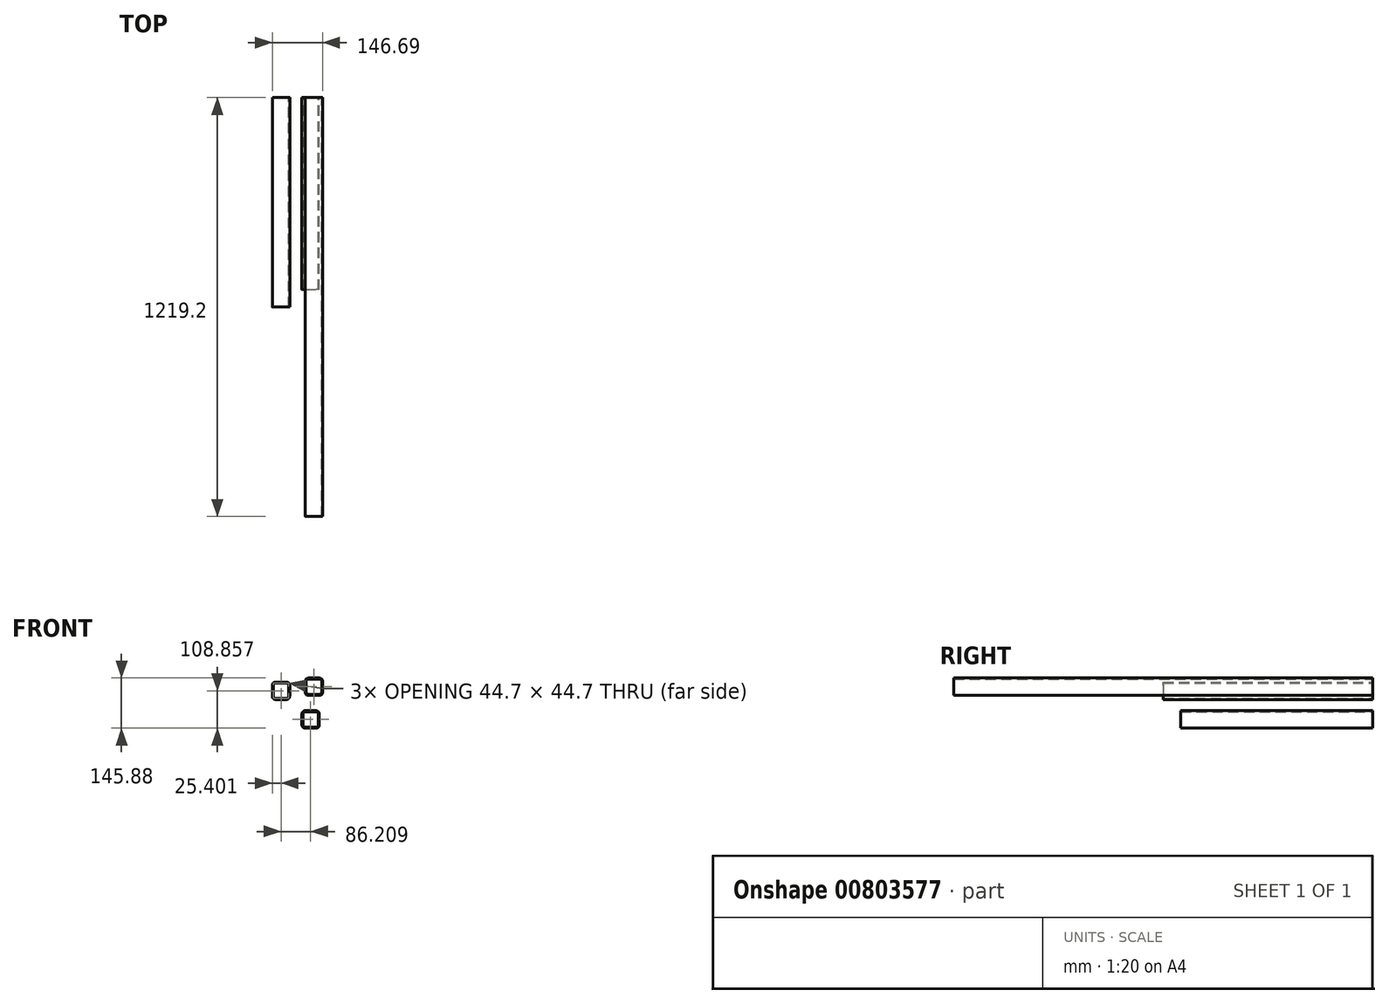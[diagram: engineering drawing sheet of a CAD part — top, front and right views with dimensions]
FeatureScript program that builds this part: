
annotation { "Feature Type Name" : "Feature", "Feature Type Description" : "" }
export const myFeature = defineFeature(function(context is Context, id is Id, definition is map)
    precondition{}
    {
        {
            var Q0;
            Q0=qCreatedBy(makeId("Front.planeOp"),FACE);
            var sketch = newSketch(context, id + "F0", { "sketchPlane" : qUnion([Q0])});
            skLineSegment(sketch, "E0.bottom", {"start": v(-72.95, 63.8) * mm, "end": v(-41.2, 63.8) * mm});
            skLineSegment(sketch, "E0.top", {"start": v(-72.95, 13) * mm, "end": v(-41.2, 13) * mm});
            skLineSegment(sketch, "E0.left", {"start": v(-82.48, 54.28) * mm, "end": v(-82.48, 22.53) * mm});
            skLineSegment(sketch, "E0.right", {"start": v(-31.68, 54.28) * mm, "end": v(-31.68, 22.53) * mm});
            skPoint(sketch, "E1.visualSharp", {"position": v(-82.48, 63.8) * mm});
            skArc(sketch, "E1.filletArc", {"start": v(-72.95, 63.8) * mm, "mid": v(-79.69, 61.02) * mm, "end": v(-82.48, 54.28) * mm});
            skPoint(sketch, "E2.visualSharp", {"position": v(-31.68, 63.8) * mm});
            skArc(sketch, "E2.filletArc", {"start": v(-31.68, 54.28) * mm, "mid": v(-34.47, 61.02) * mm, "end": v(-41.2, 63.8) * mm});
            skPoint(sketch, "E3.visualSharp", {"position": v(-31.68, 13) * mm});
            skArc(sketch, "E3.filletArc", {"start": v(-41.2, 13) * mm, "mid": v(-34.47, 15.8) * mm, "end": v(-31.68, 22.53) * mm});
            skPoint(sketch, "E4.visualSharp", {"position": v(-82.48, 13) * mm});
            skArc(sketch, "E4.filletArc", {"start": v(-82.48, 22.53) * mm, "mid": v(-79.69, 15.8) * mm, "end": v(-72.95, 13) * mm});
            skLineSegment(sketch, "E5.0", {"start": v(-72.95, 60.76) * mm, "end": v(-41.2, 60.76) * mm});
            skArc(sketch, "E6.0", {"start": v(-34.73, 54.28) * mm, "mid": v(-36.62, 58.86) * mm, "end": v(-41.2, 60.76) * mm});
            skArc(sketch, "E7.0", {"start": v(-72.95, 60.76) * mm, "mid": v(-77.53, 58.86) * mm, "end": v(-79.43, 54.28) * mm});
            skLineSegment(sketch, "E7.1", {"start": v(-79.43, 54.28) * mm, "end": v(-79.43, 22.53) * mm});
            skLineSegment(sketch, "E7.2", {"start": v(-34.73, 54.28) * mm, "end": v(-34.73, 22.53) * mm});
            skArc(sketch, "E7.3", {"start": v(-41.2, 16.05) * mm, "mid": v(-36.62, 17.95) * mm, "end": v(-34.73, 22.53) * mm});
            skLineSegment(sketch, "E7.4", {"start": v(-72.95, 16.05) * mm, "end": v(-41.2, 16.05) * mm});
            skArc(sketch, "E7.5", {"start": v(-79.43, 22.53) * mm, "mid": v(-77.53, 17.95) * mm, "end": v(-72.95, 16.05) * mm});
            skSolve(sketch);
        }
        {
            var Q0;
            Q0=makeQuery(id+"F0.imprint","IMPRINT",FACE,{"disambiguationData":[TD([[makeQuery(id+"F0.imprint","IMPRINT",EDGE,{"derivedFrom":sQuery(id+"F0.wireOp",EDGE,"E0.bottom")}),-1.0]])]});
            extrude(context, id + "F1", {"entities" : qUnion([Q0]), "depth" : 609.6 * mm, "offsetDistance" : 25.4 * mm});
        }
        {
            var Q0;
            Q0=qCreatedBy(makeId("Front.planeOp"),FACE);
            var sketch = newSketch(context, id + "F2", { "sketchPlane" : qUnion([Q0])});
            skLineSegment(sketch, "E8.bottom", {"start": v(22.93, 75.43) * mm, "end": v(54.68, 75.43) * mm});
            skLineSegment(sketch, "E8.top", {"start": v(22.93, 24.63) * mm, "end": v(54.68, 24.63) * mm});
            skLineSegment(sketch, "E8.left", {"start": v(13.4, 65.9) * mm, "end": v(13.4, 34.15) * mm});
            skLineSegment(sketch, "E8.right", {"start": v(64.2, 65.9) * mm, "end": v(64.2, 34.15) * mm});
            skPoint(sketch, "E9.visualSharp", {"position": v(13.4, 75.43) * mm});
            skArc(sketch, "E9.filletArc", {"start": v(22.93, 75.43) * mm, "mid": v(16.2, 72.64) * mm, "end": v(13.4, 65.9) * mm});
            skPoint(sketch, "E10.visualSharp", {"position": v(64.2, 75.43) * mm});
            skArc(sketch, "E10.filletArc", {"start": v(64.2, 65.9) * mm, "mid": v(61.42, 72.64) * mm, "end": v(54.68, 75.43) * mm});
            skPoint(sketch, "E11.visualSharp", {"position": v(64.2, 24.63) * mm});
            skArc(sketch, "E11.filletArc", {"start": v(54.68, 24.63) * mm, "mid": v(61.42, 27.42) * mm, "end": v(64.2, 34.15) * mm});
            skPoint(sketch, "E12.visualSharp", {"position": v(13.4, 24.63) * mm});
            skArc(sketch, "E12.filletArc", {"start": v(13.4, 34.15) * mm, "mid": v(16.2, 27.42) * mm, "end": v(22.93, 24.63) * mm});
            skLineSegment(sketch, "E13.0", {"start": v(22.93, 72.38) * mm, "end": v(54.68, 72.38) * mm});
            skArc(sketch, "E14.0", {"start": v(61.16, 65.9) * mm, "mid": v(59.26, 70.48) * mm, "end": v(54.68, 72.38) * mm});
            skArc(sketch, "E15.0", {"start": v(22.93, 72.38) * mm, "mid": v(18.35, 70.48) * mm, "end": v(16.45, 65.9) * mm});
            skLineSegment(sketch, "E15.1", {"start": v(16.45, 65.9) * mm, "end": v(16.45, 34.15) * mm});
            skLineSegment(sketch, "E15.2", {"start": v(61.16, 65.9) * mm, "end": v(61.16, 34.15) * mm});
            skArc(sketch, "E15.3", {"start": v(54.68, 27.68) * mm, "mid": v(59.26, 29.57) * mm, "end": v(61.16, 34.15) * mm});
            skLineSegment(sketch, "E15.4", {"start": v(22.93, 27.68) * mm, "end": v(54.68, 27.68) * mm});
            skArc(sketch, "E15.5", {"start": v(16.45, 34.15) * mm, "mid": v(18.35, 29.57) * mm, "end": v(22.93, 27.68) * mm});
            skSolve(sketch);
        }
        {
            var Q0;
            Q0=makeQuery(id+"F2.imprint","IMPRINT",FACE,{"disambiguationData":[TD([[makeQuery(id+"F2.imprint","IMPRINT",EDGE,{"derivedFrom":sQuery(id+"F2.wireOp",EDGE,"E8.bottom")}),-1.0]])]});
            extrude(context, id + "F3", {"entities" : qUnion([Q0]), "depth" : 1219.2 * mm, "offsetDistance" : 25.4 * mm});
        }
        {
            var Q0;
            Q0=qCreatedBy(makeId("Front.planeOp"),FACE);
            var sketch = newSketch(context, id + "F4", { "sketchPlane" : qUnion([Q0])});
            skLineSegment(sketch, "E16.bottom", {"start": v(13.25, -19.65) * mm, "end": v(45, -19.65) * mm});
            skLineSegment(sketch, "E16.top", {"start": v(13.25, -70.45) * mm, "end": v(45, -70.45) * mm});
            skLineSegment(sketch, "E16.left", {"start": v(3.73, -29.17) * mm, "end": v(3.73, -60.92) * mm});
            skLineSegment(sketch, "E16.right", {"start": v(54.53, -29.17) * mm, "end": v(54.53, -60.92) * mm});
            skPoint(sketch, "E17.visualSharp", {"position": v(3.73, -19.65) * mm});
            skArc(sketch, "E17.filletArc", {"start": v(13.25, -19.65) * mm, "mid": v(6.52, -22.43) * mm, "end": v(3.73, -29.17) * mm});
            skPoint(sketch, "E18.visualSharp", {"position": v(54.53, -19.65) * mm});
            skArc(sketch, "E18.filletArc", {"start": v(54.53, -29.17) * mm, "mid": v(51.74, -22.43) * mm, "end": v(45, -19.65) * mm});
            skPoint(sketch, "E19.visualSharp", {"position": v(54.53, -70.45) * mm});
            skArc(sketch, "E19.filletArc", {"start": v(45, -70.45) * mm, "mid": v(51.74, -67.66) * mm, "end": v(54.53, -60.92) * mm});
            skPoint(sketch, "E20.visualSharp", {"position": v(3.73, -70.45) * mm});
            skArc(sketch, "E20.filletArc", {"start": v(3.73, -60.92) * mm, "mid": v(6.52, -67.66) * mm, "end": v(13.25, -70.45) * mm});
            skLineSegment(sketch, "E21.0", {"start": v(13.25, -22.7) * mm, "end": v(45, -22.7) * mm});
            skArc(sketch, "E22.0", {"start": v(51.48, -29.17) * mm, "mid": v(49.58, -24.6) * mm, "end": v(45, -22.7) * mm});
            skArc(sketch, "E23.0", {"start": v(13.25, -22.7) * mm, "mid": v(8.67, -24.6) * mm, "end": v(6.78, -29.17) * mm});
            skLineSegment(sketch, "E23.1", {"start": v(6.78, -29.17) * mm, "end": v(6.78, -60.92) * mm});
            skLineSegment(sketch, "E23.2", {"start": v(51.48, -29.17) * mm, "end": v(51.48, -60.92) * mm});
            skArc(sketch, "E23.3", {"start": v(45, -67.4) * mm, "mid": v(49.58, -65.5) * mm, "end": v(51.48, -60.92) * mm});
            skLineSegment(sketch, "E23.4", {"start": v(13.25, -67.4) * mm, "end": v(45, -67.4) * mm});
            skArc(sketch, "E23.5", {"start": v(6.78, -60.92) * mm, "mid": v(8.67, -65.5) * mm, "end": v(13.25, -67.4) * mm});
            skSolve(sketch);
        }
        {
            var Q0;
            Q0=makeQuery(id+"F4.imprint","IMPRINT",FACE,{"disambiguationData":[TD([[makeQuery(id+"F4.imprint","IMPRINT",EDGE,{"derivedFrom":sQuery(id+"F4.wireOp",EDGE,"E16.bottom")}),-1.0]])]});
            extrude(context, id + "F5", {"entities" : qUnion([Q0]), "depth" : 558.8 * mm, "offsetDistance" : 25.4 * mm});
        }
    });
